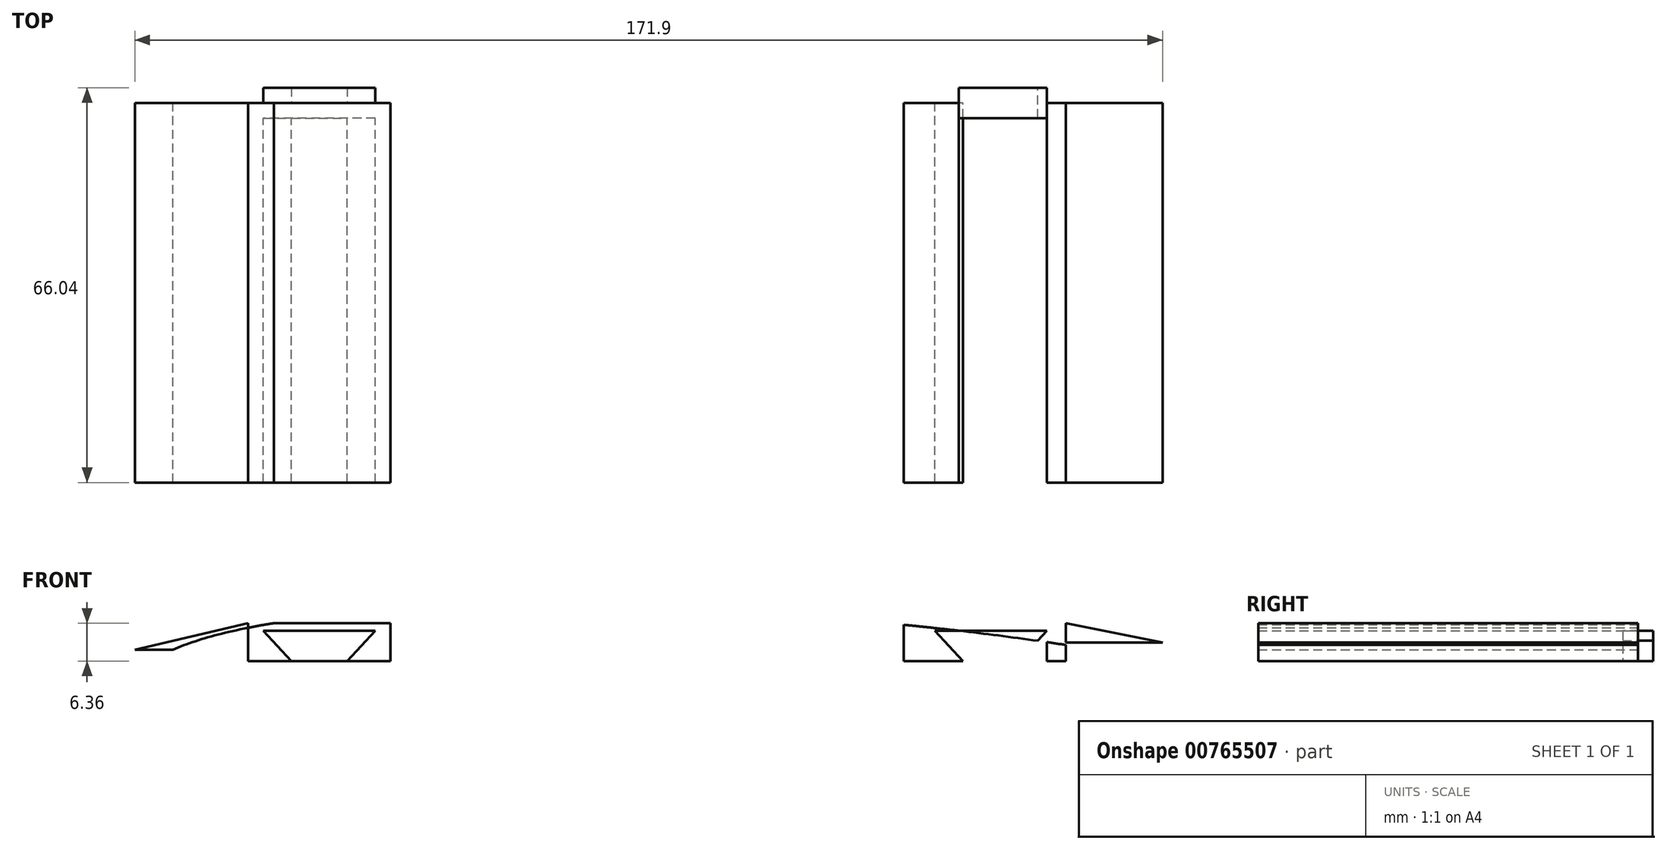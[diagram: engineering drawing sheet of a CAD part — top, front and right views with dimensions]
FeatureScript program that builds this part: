
annotation { "Feature Type Name" : "Feature", "Feature Type Description" : "" }
export const myFeature = defineFeature(function(context is Context, id is Id, definition is map)
    precondition{}
    {
        {
            var Q0;
            Q0=qCreatedBy(makeId("Front.planeOp"),FACE);
            var sketch = newSketch(context, id + "F0", { "sketchPlane" : qUnion([Q0])});
            skLineSegment(sketch, "E0.bottom", {"start": v(127, -127) * mm, "end": v(-127, -127) * mm});
            skLineSegment(sketch, "E0.top", {"start": v(127, 127) * mm, "end": v(-127, 127) * mm});
            skLineSegment(sketch, "E0.left", {"start": v(127, -127) * mm, "end": v(127, 127) * mm});
            skLineSegment(sketch, "E0.right", {"start": v(-127, -127) * mm, "end": v(-127, 127) * mm});
            skPoint(sketch, "E0.middle", {"position": v(0, 0) * mm});
            skFitSpline(sketch, "E1", {"points": [v(-91.31, -6.35) * mm, v(-40.51, -44.45) * mm, v(111.89, -19.04) * mm, v(-91.31, -6.35) * mm]});
            skLineSegment(sketch, "E2", {"start": v(-40.51, -44.45) * mm, "end": v(-15.3, -47.27) * mm});
            skLineSegment(sketch, "E3", {"start": v(27.81, -46.66) * mm, "end": v(11.65, -47.54) * mm});
            skLineSegment(sketch, "E4", {"start": v(27.81, -46.66) * mm, "end": v(53.06, -43.86) * mm});
            skFitSpline(sketch, "E5.0", {"points": [v(-91.09, -2.49) * mm, v(-93.11, -3.68) * mm, v(-94.9, -5.02) * mm, v(-96.4, -6.5) * mm, v(-97.63, -8.14) * mm, v(-98.53, -9.94) * mm, v(-99.08, -11.85) * mm, v(-99.25, -13.81) * mm, v(-99.06, -15.77) * mm, v(-98.4, -18.3) * mm, v(-96.87, -21.31) * mm, v(-94.16, -24.73) * mm, v(-90.64, -28.01) * mm, v(-86.36, -31.18) * mm, v(-81.36, -34.22) * mm, v(-73.8, -38.07) * mm, v(-64.96, -41.56) * mm, v(-55.02, -44.53) * mm, v(-47.07, -46.47) * mm, v(-38.66, -48.06) * mm, v(-29.88, -49.27) * mm, v(-20.78, -50.14) * mm, v(-8.34, -50.87) * mm, v(7.62, -51) * mm, v(26.86, -50.08) * mm, v(45.6, -48.22) * mm, v(63.29, -45.58) * mm, v(76.65, -42.83) * mm, v(86.23, -40.36) * mm, v(92.8, -38.4) * mm, v(98.69, -36.33) * mm, v(103.83, -34.17) * mm, v(108.19, -31.9) * mm, v(111.13, -29.88) * mm, v(113.07, -28.12) * mm, v(114.3, -26.7) * mm, v(115.27, -25.1) * mm, v(115.91, -23.32) * mm, v(116.1, -21.37) * mm, v(115.72, -19.41) * mm, v(115, -17.94) * mm, v(114.25, -16.88) * mm, v(113.4, -15.9) * mm, v(112.17, -14.78) * mm, v(110.46, -13.57) * mm, v(108.52, -12.43) * mm, v(105.62, -11) * mm, v(101.4, -9.3) * mm, v(95.44, -7.37) * mm, v(88.64, -5.55) * mm, v(81.1, -3.85) * mm, v(72.86, -2.25) * mm, v(61.11, -0.27) * mm, v(45.17, 1.89) * mm, v(24.75, 3.92) * mm, v(3.78, 5.34) * mm, v(-17.03, 6.07) * mm, v(-36.93, 6.04) * mm, v(-52.18, 5.32) * mm, v(-63.21, 4.3) * mm, v(-70.83, 3.28) * mm, v(-77.7, 2.02) * mm, v(-83.76, 0.48) * mm, v(-88.08, -1.06) * mm, v(-91.09, -2.49) * mm, v(-93.11, -3.68) * mm, v(-94.9, -5.02) * mm]});
            skLineSegment(sketch, "E6", {"start": v(-48.23, -4.6) * mm, "end": v(-48.23, 0) * mm});
            skLineSegment(sketch, "E7", {"start": v(-48.23, 0) * mm, "end": v(-94.09, 0) * mm});
            skLineSegment(sketch, "E8", {"start": v(-94.09, 0) * mm, "end": v(-94.09, -4.43) * mm});
            skLineSegment(sketch, "E9", {"start": v(34.52, -6.34) * mm, "end": v(34.52, 0.01) * mm});
            skLineSegment(sketch, "E10", {"start": v(34.52, 0.01) * mm, "end": v(77.81, 0.01) * mm});
            skLineSegment(sketch, "E11", {"start": v(77.81, 0.01) * mm, "end": v(77.81, -3.22) * mm});
            skPoint(sketch, "E12", {"position": v(-88.1, 0) * mm});
            skPoint(sketch, "E13", {"position": v(77.2, 0.01) * mm});
            skLineSegment(sketch, "E14", {"start": v(77.2, -6.34) * mm, "end": v(58.47, -6.34) * mm});
            skLineSegment(sketch, "E15", {"start": v(39.75, -6.34) * mm, "end": v(39.75, 0.01) * mm});
            skLineSegment(sketch, "E16", {"start": v(58.47, -6.34) * mm, "end": v(58.47, 0.01) * mm});
            skLineSegment(sketch, "E17.top", {"start": v(58.47, -1.26) * mm, "end": v(39.75, -1.26) * mm});
            skLineSegment(sketch, "E17.left", {"start": v(58.47, -6.34) * mm, "end": v(58.47, -1.26) * mm});
            skLineSegment(sketch, "E17.right", {"start": v(39.75, -6.34) * mm, "end": v(39.75, -1.26) * mm});
            skLineSegment(sketch, "E18", {"start": v(34.52, -6.34) * mm, "end": v(39.75, -6.34) * mm});
            skPoint(sketch, "E19.endSnap0", {"position": v(49.11, -1.26) * mm});
            skPoint(sketch, "E20", {"position": v(53.8, -6.34) * mm});
            skPoint(sketch, "E21", {"position": v(44.43, -6.34) * mm});
            skLineSegment(sketch, "E22", {"start": v(58.47, -6.34) * mm, "end": v(39.75, -6.34) * mm});
            skLineSegment(sketch, "E23", {"start": v(58.47, -1.26) * mm, "end": v(53.8, -6.34) * mm});
            skLineSegment(sketch, "E24", {"start": v(39.75, -1.26) * mm, "end": v(44.43, -6.34) * mm});
            skLineSegment(sketch, "E25", {"start": v(-91.31, -6.35) * mm, "end": v(-48.23, -6.35) * mm});
            skLineSegment(sketch, "E26", {"start": v(-48.23, -6.35) * mm, "end": v(-48.23, -4.6) * mm});
            skLineSegment(sketch, "E27", {"start": v(77.81, -3.22) * mm, "end": v(61.63, -3.22) * mm});
            skLineSegment(sketch, "E28", {"start": v(61.63, 0.01) * mm, "end": v(61.63, -6.34) * mm});
            skLineSegment(sketch, "E29", {"start": v(-94.09, -4.43) * mm, "end": v(-77.9, -4.43) * mm});
            skLineSegment(sketch, "E30", {"start": v(37.21, 0.01) * mm, "end": v(37.21, -6.34) * mm});
            skLineSegment(sketch, "E31", {"start": v(37.21, -3.8) * mm, "end": v(34.52, -3.8) * mm});
            skLineSegment(sketch, "E32", {"start": v(-72.6, -6.35) * mm, "end": v(-72.6, 0) * mm});
            skLineSegment(sketch, "E33.top", {"start": v(-53.87, -1.27) * mm, "end": v(-72.6, -1.27) * mm});
            skLineSegment(sketch, "E34", {"start": v(-53.87, -1.27) * mm, "end": v(-58.55, -6.35) * mm});
            skLineSegment(sketch, "E35", {"start": v(-72.6, -1.27) * mm, "end": v(-67.91, -6.35) * mm});
            skLineSegment(sketch, "E36", {"start": v(-53.87, -6.35) * mm, "end": v(-53.87, 0) * mm});
            skLineSegment(sketch, "E37", {"start": v(-51.33, -6.35) * mm, "end": v(-51.33, 0) * mm});
            skLineSegment(sketch, "E38", {"start": v(-72.6, -3.17) * mm, "end": v(-75.13, -3.17) * mm});
            skLineSegment(sketch, "E39", {"start": v(-75.13, 0) * mm, "end": v(-75.13, -6.35) * mm});
            skLineSegment(sketch, "E40", {"start": v(-77.9, -4.43) * mm, "end": v(-75.13, -4.43) * mm});
            skPoint(sketch, "E41.1.internal.snap0", {"position": v(69.72, -3.22) * mm});
            skPoint(sketch, "E41.1.internal.snap1", {"position": v(77.81, -1.6) * mm});
            skLineSegment(sketch, "E42", {"start": v(77.81, -3.22) * mm, "end": v(61.63, 0.01) * mm});
            skLineSegment(sketch, "E43", {"start": v(-94.09, -4.43) * mm, "end": v(-75.13, 0) * mm});
            skSolve(sketch);
        }
        {
            var Q0;
            {var subQ5=sQuery(id+"F0.wireOp",EDGE,"E33.top");Q0=makeQuery(id+"F0.imprint","IMPRINT",FACE,{"disambiguationData":[TD([[makeQuery(id+"F0.imprint","IMPRINT",EDGE,{"derivedFrom":subQ5}),-1.0]])]});}
            var Q1;
            Q1=makeQuery(id+"F0.imprint","IMPRINT",FACE,{"disambiguationData":[TD([[makeQuery(id+"F0.imprint","IMPRINT",EDGE,{"derivedFrom":sQuery(id+"F0.wireOp",EDGE,"E5.0")}),1.0]])]});
            var Q2;
            {var subQ0=sQuery(id+"F0.wireOp",EDGE,"E32");var subQ1=sQuery(id+"F0.wireOp",EDGE,"E25");var subQ2=makeQuery(id+"F0.imprint","INTERSECT",VERTEX,{"derivedFrom":[subQ1,subQ0]});Q2=makeQuery(id+"F0.imprint","IMPRINT",FACE,{"disambiguationData":[TD([[makeQuery(id+"F0.imprint","IMPRINT",EDGE,{"disambiguationData":[TD([[subQ2,-1.0]])],"derivedFrom":subQ1}),1.0]])]});}
            var Q3;
            {var subQ0=sQuery(id+"F0.wireOp",EDGE,"E34");Q3=makeQuery(id+"F0.imprint","IMPRINT",FACE,{"disambiguationData":[TD([[makeQuery(id+"F0.imprint","IMPRINT",EDGE,{"derivedFrom":subQ0}),1.0]])]});}
            var Q4;
            {var subQ1=sQuery(id+"F0.wireOp",EDGE,"E16");Q4=makeQuery(id+"F0.imprint","IMPRINT",FACE,{"disambiguationData":[TD([[makeQuery(id+"F0.imprint","IMPRINT",EDGE,{"derivedFrom":subQ1}),-1.0]])]});}
            var Q5;
            {var subQ4=sQuery(id+"F0.wireOp",EDGE,"E37");Q5=makeQuery(id+"F0.imprint","IMPRINT",FACE,{"disambiguationData":[TD([[makeQuery(id+"F0.imprint","IMPRINT",EDGE,{"derivedFrom":subQ4}),1.0]])]});}
            var Q6;
            {var subQ0=sQuery(id+"F0.wireOp",EDGE,"E38");Q6=makeQuery(id+"F0.imprint","IMPRINT",FACE,{"disambiguationData":[TD([[makeQuery(id+"F0.imprint","IMPRINT",EDGE,{"derivedFrom":subQ0}),-1.0]])]});}
            var Q7;
            {var subQ0=sQuery(id+"F0.wireOp",EDGE,"E38");Q7=makeQuery(id+"F0.imprint","IMPRINT",FACE,{"disambiguationData":[TD([[makeQuery(id+"F0.imprint","IMPRINT",EDGE,{"derivedFrom":subQ0}),1.0]])]});}
            var Q8;
            {var subQ3=sQuery(id+"F0.wireOp",EDGE,"E31");Q8=makeQuery(id+"F0.imprint","IMPRINT",FACE,{"disambiguationData":[TD([[makeQuery(id+"F0.imprint","IMPRINT",EDGE,{"derivedFrom":subQ3}),-1.0]])]});}
            var Q9;
            {var subQ4=sQuery(id+"F0.wireOp",EDGE,"E15");Q9=makeQuery(id+"F0.imprint","IMPRINT",FACE,{"disambiguationData":[TD([[makeQuery(id+"F0.imprint","IMPRINT",EDGE,{"derivedFrom":subQ4}),1.0]])]});}
            var Q10;
            {var subQ3=sQuery(id+"F0.wireOp",EDGE,"E31");Q10=makeQuery(id+"F0.imprint","IMPRINT",FACE,{"disambiguationData":[TD([[makeQuery(id+"F0.imprint","IMPRINT",EDGE,{"derivedFrom":subQ3}),1.0]])]});}
            var Q11;
            {var subQ5=sQuery(id+"F0.wireOp",EDGE,"E15");Q11=makeQuery(id+"F0.imprint","IMPRINT",FACE,{"disambiguationData":[TD([[makeQuery(id+"F0.imprint","IMPRINT",EDGE,{"derivedFrom":subQ5}),-1.0]])]});}
            var Q12;
            {var subQ0=sQuery(id+"F0.wireOp",EDGE,"E17.left");Q12=makeQuery(id+"F0.imprint","IMPRINT",FACE,{"disambiguationData":[TD([[makeQuery(id+"F0.imprint","IMPRINT",EDGE,{"derivedFrom":subQ0}),1.0]])]});}
            var Q13;
            {var subQ0=sQuery(id+"F0.wireOp",EDGE,"E17.right");Q13=makeQuery(id+"F0.imprint","IMPRINT",FACE,{"disambiguationData":[TD([[makeQuery(id+"F0.imprint","IMPRINT",EDGE,{"derivedFrom":subQ0}),-1.0]])]});}
            var Q14;
            {var subQ0=sQuery(id+"F0.wireOp",EDGE,"E27");Q14=makeQuery(id+"F0.imprint","IMPRINT",FACE,{"disambiguationData":[TD([[makeQuery(id+"F0.imprint","IMPRINT",EDGE,{"derivedFrom":subQ0}),-1.0]])]});}
            var Q15;
            Q15=makeQuery(id+"F0.imprint","IMPRINT",FACE,{"disambiguationData":[TD([[makeQuery(id+"F0.imprint","IMPRINT",EDGE,{"derivedFrom":sQuery(id+"F0.wireOp",EDGE,"E29")}),1.0]])]});
            extrude(context, id + "F1", {"entities" : qUnion([Q0, Q1, Q2, Q3, Q4, Q5, Q6, Q7, Q8, Q9, Q10, Q11, Q12, Q13, Q14, Q15]), "depth" : 63.5 * mm, "offsetDistance" : 25.4 * mm});
        }
        {
            var Q0;
            {var subQ0=sQuery(id+"F0.wireOp",EDGE,"E17.top");Q0=makeQuery(id+"F0.imprint","IMPRINT",FACE,{"disambiguationData":[TD([[makeQuery(id+"F0.imprint","IMPRINT",EDGE,{"derivedFrom":subQ0}),1.0]])]});}
            extrude(context, id + "F2", {"entities" : qUnion([Q0]), "operationType" : NewBodyOperationType.ADD, "depth" : 2.54 * mm, "offsetDistance" : 25.4 * mm});
        }
        {
            var Q0;
            {var subQ4=sQuery(id+"F0.wireOp",EDGE,"E33.top");Q0=makeQuery(id+"F0.imprint","IMPRINT",FACE,{"disambiguationData":[TD([[makeQuery(id+"F0.imprint","IMPRINT",EDGE,{"derivedFrom":subQ4}),1.0]])]});}
            extrude(context, id + "F3", {"entities" : qUnion([Q0]), "operationType" : NewBodyOperationType.ADD, "depth" : 2.54 * mm, "offsetDistance" : 25.4 * mm});
        }
        {
            var Q0;
            {var subQ0=sQuery(id+"F0.wireOp",EDGE,"E17.top");Q0=makeQuery(id+"F0.imprint","IMPRINT",FACE,{"disambiguationData":[TD([[makeQuery(id+"F0.imprint","IMPRINT",EDGE,{"derivedFrom":subQ0}),1.0]])]});}
            var Q1;
            {var subQ4=sQuery(id+"F0.wireOp",EDGE,"E33.top");Q1=makeQuery(id+"F0.imprint","IMPRINT",FACE,{"disambiguationData":[TD([[makeQuery(id+"F0.imprint","IMPRINT",EDGE,{"derivedFrom":subQ4}),1.0]])]});}
            extrude(context, id + "F4", {"entities" : qUnion([Q0, Q1]), "operationType" : NewBodyOperationType.ADD, "oppositeDirection" : true, "depth" : 2.54 * mm, "offsetDistance" : 25.4 * mm});
        }
    });
